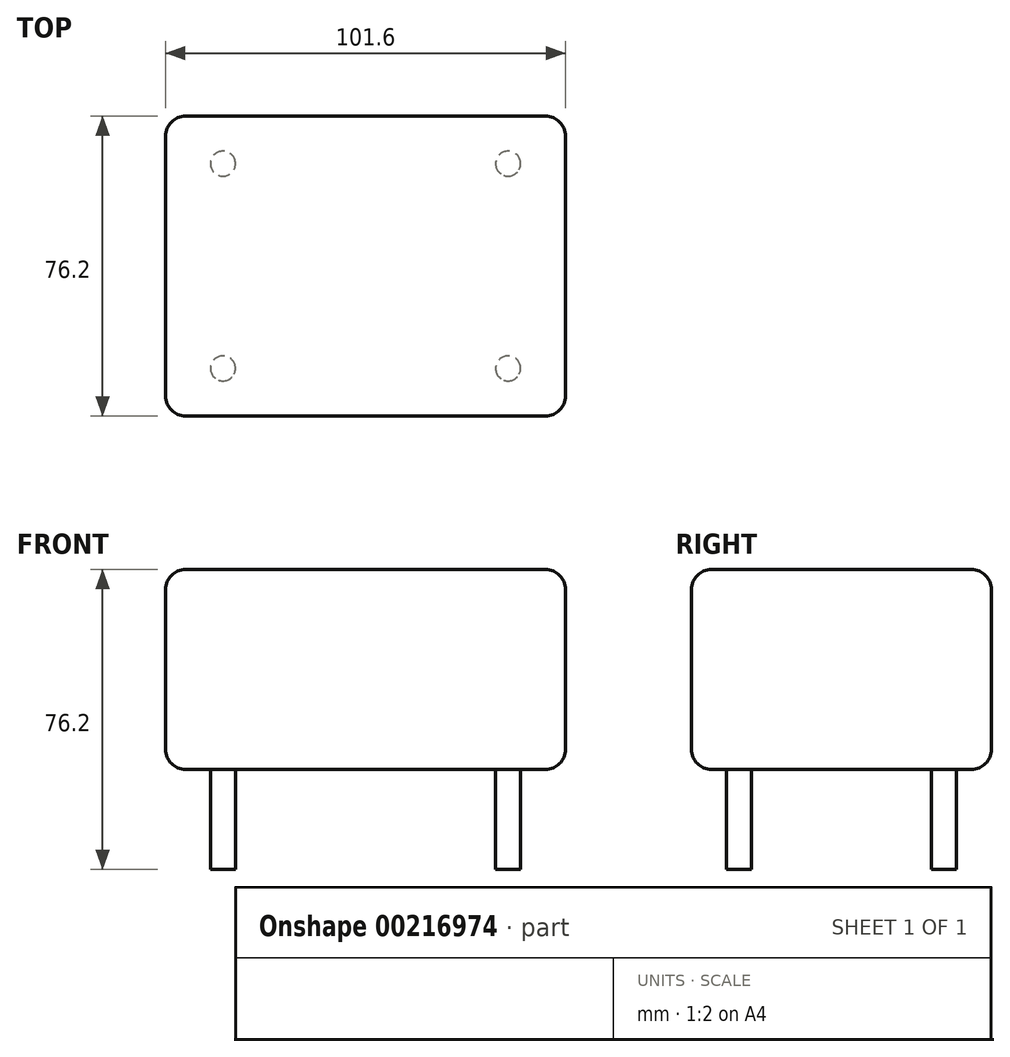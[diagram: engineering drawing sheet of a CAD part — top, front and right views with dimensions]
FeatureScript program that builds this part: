
annotation { "Feature Type Name" : "Feature", "Feature Type Description" : "" }
export const myFeature = defineFeature(function(context is Context, id is Id, definition is map)
    precondition{}
    {
        {
            var Q0;
            Q0=qCreatedBy(makeId("Top.planeOp"),FACE);
            var sketch = newSketch(context, id + "F0", { "sketchPlane" : qUnion([Q0])});
            skLineSegment(sketch, "E0.bottom", {"start": v(50.8, -38.1) * mm, "end": v(-50.8, -38.1) * mm});
            skLineSegment(sketch, "E0.top", {"start": v(50.8, 38.1) * mm, "end": v(-50.8, 38.1) * mm});
            skLineSegment(sketch, "E0.left", {"start": v(50.8, -38.1) * mm, "end": v(50.8, 38.1) * mm});
            skLineSegment(sketch, "E0.right", {"start": v(-50.8, -38.1) * mm, "end": v(-50.8, 38.1) * mm});
            skPoint(sketch, "E0.middle", {"position": v(0, 0) * mm});
            skSolve(sketch);
        }
        {
            var Q0;
            Q0=makeQuery(id+"F0.imprint","IMPRINT",FACE,{"disambiguationData":[TD([[makeQuery(id+"F0.imprint","IMPRINT",EDGE,{"derivedFrom":sQuery(id+"F0.wireOp",EDGE,"E0.bottom")}),-1.0]])]});
            extrude(context, id + "F1", {"entities" : qUnion([Q0]), "depth" : 50.8 * mm});
        }
        {
            var Q0;
            Q0=makeQuery(id+"F1.opExtrude","SWEPT_FACE",FACE,{"disambiguationData":[OSD([sQuery(id+"F0.wireOp",EDGE,"E0.bottom")])]});
            var Q1;
            Q1=makeQuery(id+"F1.opExtrude","SWEPT_FACE",FACE,{"disambiguationData":[OSD([sQuery(id+"F0.wireOp",EDGE,"E0.left")])]});
            var Q2;
            Q2=makeQuery(id+"F1.opExtrude","CAP_FACE",FACE,{"disambiguationData":[OSD([sQuery(id+"F0.wireOp",EDGE,"E0.bottom"),sQuery(id+"F0.wireOp",EDGE,"E0.top"),sQuery(id+"F0.wireOp",EDGE,"E0.left"),sQuery(id+"F0.wireOp",EDGE,"E0.right")])],"isStart":false});
            var Q3;
            Q3=makeQuery(id+"F1.opExtrude","SWEPT_FACE",FACE,{"disambiguationData":[OSD([sQuery(id+"F0.wireOp",EDGE,"E0.top")])]});
            var Q4;
            Q4=makeQuery(id+"F1.opExtrude","CAP_FACE",FACE,{"disambiguationData":[OSD([sQuery(id+"F0.wireOp",EDGE,"E0.bottom"),sQuery(id+"F0.wireOp",EDGE,"E0.top"),sQuery(id+"F0.wireOp",EDGE,"E0.left"),sQuery(id+"F0.wireOp",EDGE,"E0.right")])],"isStart":true});
            fillet(context, id + "F2", {"entities" : qUnion([Q0, Q1, Q2, Q3, Q4]), "radius" : 5.08 * mm, "tangentPropagation" : true, "allowEdgeOverflow" : false});
        }
        {
            var Q0;
            Q0=makeQuery(id+"F1.opExtrude","CAP_FACE",FACE,{"disambiguationData":[OSD([sQuery(id+"F0.wireOp",EDGE,"E0.bottom"),sQuery(id+"F0.wireOp",EDGE,"E0.top"),sQuery(id+"F0.wireOp",EDGE,"E0.left"),sQuery(id+"F0.wireOp",EDGE,"E0.right")])],"isStart":true});
            var sketch = newSketch(context, id + "F3", { "sketchPlane" : qUnion([Q0])});
            skLineSegment(sketch, "E1.bottom", {"start": v(36.22, -26.01) * mm, "end": v(-36.22, -26.01) * mm});
            skLineSegment(sketch, "E1.top", {"start": v(36.22, 26.01) * mm, "end": v(-36.22, 26.01) * mm});
            skLineSegment(sketch, "E1.left", {"start": v(36.22, -26.01) * mm, "end": v(36.22, 26.01) * mm});
            skLineSegment(sketch, "E1.right", {"start": v(-36.22, -26.01) * mm, "end": v(-36.22, 26.01) * mm});
            skPoint(sketch, "E1.middle", {"position": v(0, 0) * mm});
            skCircle(sketch, "E2", {"center": v(-36.22, -26.01) * mm, "radius": 3.18 * mm});
            skCircle(sketch, "E3", {"center": v(-36.22, 26.01) * mm, "radius": 3.18 * mm});
            skCircle(sketch, "E4", {"center": v(36.22, 26.01) * mm, "radius": 3.18 * mm});
            skCircle(sketch, "E5", {"center": v(36.22, -26.01) * mm, "radius": 3.18 * mm});
            skSolve(sketch);
        }
        {
            var Q0;
            {var subQ0=sQuery(id+"F3.wireOp",EDGE,"E1.left");var subQ1=sQuery(id+"F3.wireOp",EDGE,"E1.bottom");var subQ2=makeQuery(id+"F3.imprint","INTERSECT",VERTEX,{"derivedFrom":[subQ1,subQ0]});Q0=makeQuery(id+"F3.imprint","IMPRINT",FACE,{"disambiguationData":[TD([[makeQuery(id+"F3.imprint","IMPRINT",EDGE,{"disambiguationData":[TD([[subQ2,-1.0]])],"derivedFrom":subQ1}),1.0]])]});}
            var Q1;
            {var subQ0=sQuery(id+"F3.wireOp",EDGE,"E1.left");var subQ1=sQuery(id+"F3.wireOp",EDGE,"E1.bottom");var subQ2=makeQuery(id+"F3.imprint","INTERSECT",VERTEX,{"derivedFrom":[subQ1,subQ0]});Q1=makeQuery(id+"F3.imprint","IMPRINT",FACE,{"disambiguationData":[TD([[makeQuery(id+"F3.imprint","IMPRINT",EDGE,{"disambiguationData":[TD([[subQ2,-1.0]])],"derivedFrom":subQ1}),-1.0]])]});}
            var Q2;
            {var subQ0=sQuery(id+"F3.wireOp",EDGE,"E1.left");var subQ1=sQuery(id+"F3.wireOp",EDGE,"E1.top");var subQ2=makeQuery(id+"F3.imprint","INTERSECT",VERTEX,{"derivedFrom":[subQ1,subQ0]});Q2=makeQuery(id+"F3.imprint","IMPRINT",FACE,{"disambiguationData":[TD([[makeQuery(id+"F3.imprint","IMPRINT",EDGE,{"disambiguationData":[TD([[subQ2,-1.0]])],"derivedFrom":subQ1}),1.0]])]});}
            var Q3;
            {var subQ0=sQuery(id+"F3.wireOp",EDGE,"E1.left");var subQ1=sQuery(id+"F3.wireOp",EDGE,"E1.top");var subQ2=makeQuery(id+"F3.imprint","INTERSECT",VERTEX,{"derivedFrom":[subQ1,subQ0]});Q3=makeQuery(id+"F3.imprint","IMPRINT",FACE,{"disambiguationData":[TD([[makeQuery(id+"F3.imprint","IMPRINT",EDGE,{"disambiguationData":[TD([[subQ2,-1.0]])],"derivedFrom":subQ1}),-1.0]])]});}
            var Q4;
            {var subQ0=sQuery(id+"F3.wireOp",EDGE,"E1.right");var subQ1=sQuery(id+"F3.wireOp",EDGE,"E1.top");var subQ2=makeQuery(id+"F3.imprint","INTERSECT",VERTEX,{"derivedFrom":[subQ1,subQ0]});Q4=makeQuery(id+"F3.imprint","IMPRINT",FACE,{"disambiguationData":[TD([[makeQuery(id+"F3.imprint","IMPRINT",EDGE,{"disambiguationData":[TD([[subQ2,1.0]])],"derivedFrom":subQ1}),1.0]])]});}
            var Q5;
            {var subQ0=sQuery(id+"F3.wireOp",EDGE,"E1.right");var subQ1=sQuery(id+"F3.wireOp",EDGE,"E1.top");var subQ2=makeQuery(id+"F3.imprint","INTERSECT",VERTEX,{"derivedFrom":[subQ1,subQ0]});Q5=makeQuery(id+"F3.imprint","IMPRINT",FACE,{"disambiguationData":[TD([[makeQuery(id+"F3.imprint","IMPRINT",EDGE,{"disambiguationData":[TD([[subQ2,1.0]])],"derivedFrom":subQ1}),-1.0]])]});}
            var Q6;
            {var subQ0=sQuery(id+"F3.wireOp",EDGE,"E1.right");var subQ1=sQuery(id+"F3.wireOp",EDGE,"E1.bottom");var subQ2=makeQuery(id+"F3.imprint","INTERSECT",VERTEX,{"derivedFrom":[subQ1,subQ0]});Q6=makeQuery(id+"F3.imprint","IMPRINT",FACE,{"disambiguationData":[TD([[makeQuery(id+"F3.imprint","IMPRINT",EDGE,{"disambiguationData":[TD([[subQ2,1.0]])],"derivedFrom":subQ1}),-1.0]])]});}
            var Q7;
            {var subQ0=sQuery(id+"F3.wireOp",EDGE,"E1.right");var subQ1=sQuery(id+"F3.wireOp",EDGE,"E1.bottom");var subQ2=makeQuery(id+"F3.imprint","INTERSECT",VERTEX,{"derivedFrom":[subQ1,subQ0]});Q7=makeQuery(id+"F3.imprint","IMPRINT",FACE,{"disambiguationData":[TD([[makeQuery(id+"F3.imprint","IMPRINT",EDGE,{"disambiguationData":[TD([[subQ2,1.0]])],"derivedFrom":subQ1}),1.0]])]});}
            extrude(context, id + "F4", {"entities" : qUnion([Q0, Q1, Q2, Q3, Q4, Q5, Q6, Q7]), "operationType" : NewBodyOperationType.ADD, "depth" : 25.4 * mm});
        }
    });
